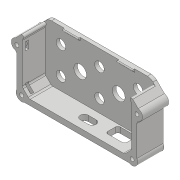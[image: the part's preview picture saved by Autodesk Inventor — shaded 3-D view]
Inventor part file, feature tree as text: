
AUTODESK INVENTOR PART (.ipt)
format: ipt  version: 2017.3 (Build 213257000, 257)  size: 408,064 bytes
history: native  units: mm
features: extrude x10, sketch x9, reference x9, projected_geometry x8, other x6, plane x1
ambient origin geometry x8: Origin, YZ Plane, XZ Plane, XY Plane, X Axis, Y Axis, Z Axis, Center Point
bodies: Solid1 (feature_tree)
feature tree (43):
  other  "Cover Flir One Pro.ipt"
  plane  "Work Plane1"
  extrude  "Extrusion1"  [1 undecoded]
  extrude  "Extrusion4"  Depth=1.91mm TaperAngle=0.0deg
  extrude  "Extrusion6"  Depth=0.05mm
  extrude  "Extrusion7"  Depth=3.91mm TaperAngle=0.0deg
  extrude  "Extrusion8"  Depth=10.0mm TaperAngle=0.0deg
  extrude  "Extrusion9"  Depth=7.0mm
  extrude  "Extrusion11"  Depth=0.05mm TaperAngle=0.0deg
  extrude  "Extrusion12"  Depth=12.0mm TaperAngle=0.0deg
  extrude  "Extrusion13"  Depth=5.0mm
  extrude  "Extrusion14"  Depth=10.0mm
  other  "Solid2::Cover Flir One Pro.ipt"
  other  "TaggingFeature1"
  sketch  "Sketch4"  dims[d0=10.0mm d1=-2.0mm]
  projected_geometry  "Projected Loop1"
  projected_geometry  "Projected Loop2"
  sketch  "Sketch6"  dims[d2=5.0mm d4=1.91mm d5=0.0mm]
  reference  "Reference13"
  reference  "Reference14"
  reference  "Reference15"
  reference  "Reference16"
  reference  "Reference17"
  reference  "Reference18"
  reference  "Reference19"
  sketch  "Sketch7"  dims[d14=0.05mm d15=0.0mm d18=7.0mm]
  reference  "Reference20"
  reference  "Reference21"
  sketch  "Sketch8"  dims[d19=7.0mm d20=3.91mm d21=12.565mm d22=0.0mm d23=0.0mm]
  sketch  "Sketch9"  dims[d24=3.91mm d25=0.0mm d28=10.0mm d29=0.0mm]
  sketch  "Sketch11"  dims[d30=7.0mm d31=7.0mm]
  projected_geometry  "Projected Loop7"
  projected_geometry  "Projected Loop8"
  sketch  "Sketch12"  dims[d32=3.91mm d33=12.56mm d34=0.0mm d35=0.0mm d38=0.05mm d39=0.0mm]
  sketch  "Sketch13"  dims[d40=2.5mm d41=12.0mm d42=0.0mm]
  projected_geometry  "Projected Loop9"
  projected_geometry  "Projected Loop10"
  sketch  "Sketch14"  dims[d43=10.0mm d44=5.0mm d45=7.1mm d48=12.0mm d49=7.8mm d50=1.5mm d54=10.0mm d55=0.0mm d56=10.879mm d57=13.25mm d58=10.0mm d59=0.0mm]
  projected_geometry  "Projected Loop11"
  projected_geometry  "Projected Loop12"
  parser-record x1  (decoder bookkeeping rows leaked as tree rows — omitted from the tree; the rows remain in map.json)
  other  "Assembly1.iam"
  other  "CoverPart2:1"
note: 1 required parameter value undecoded (feature->parameter linkage not recoverable at this tier; creation-order binding heuristic only, values carry confidence <= 0.55)
note: 1 file-system path scrubbed to <path> (originals preserved in map.json)
